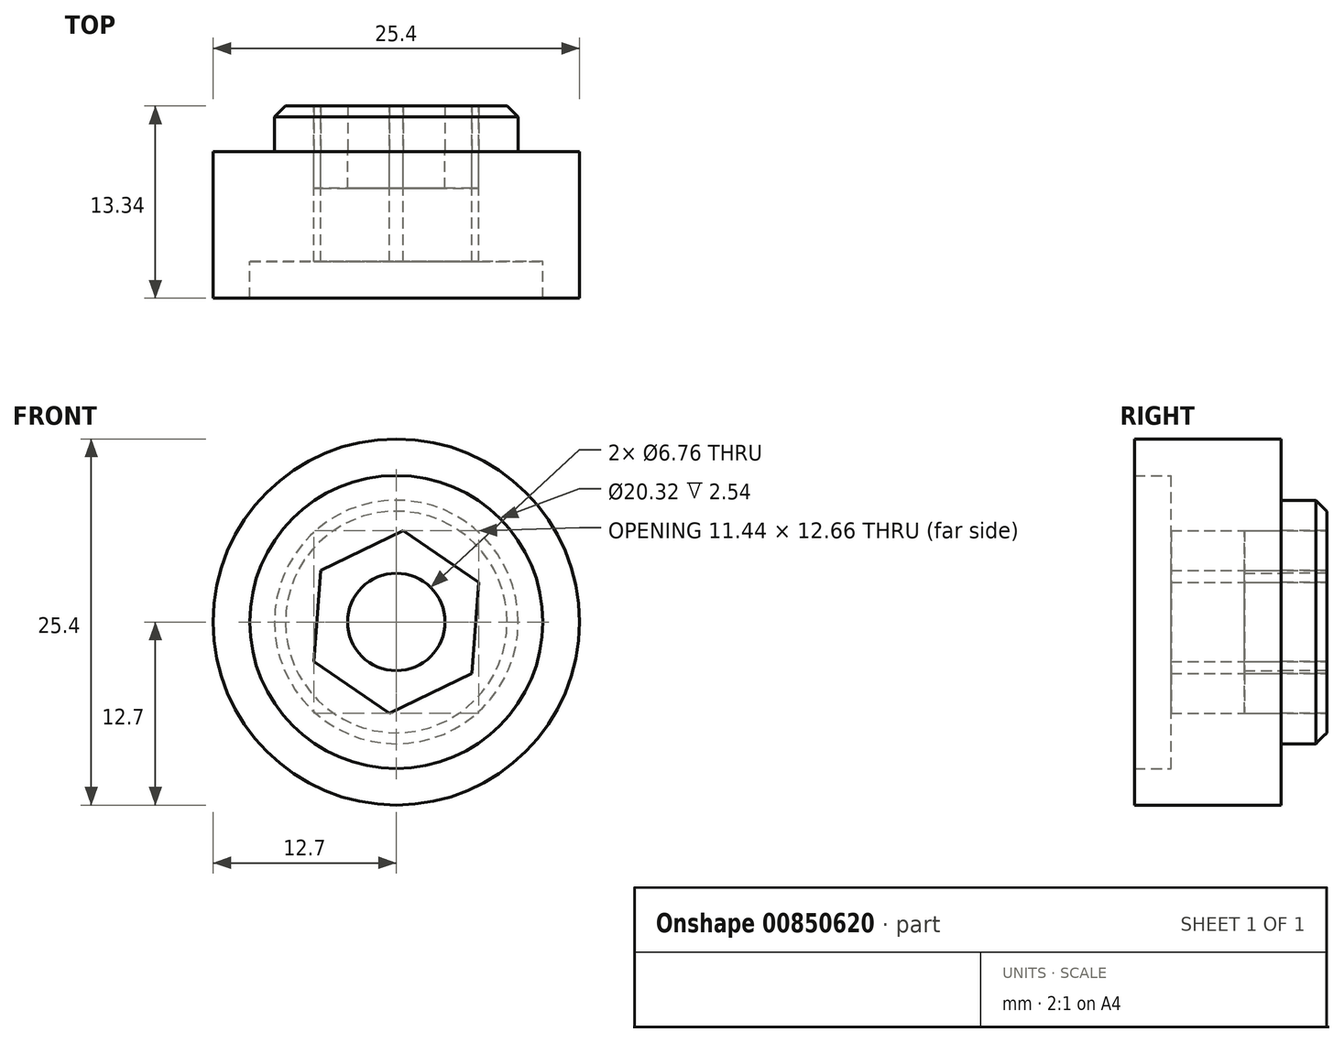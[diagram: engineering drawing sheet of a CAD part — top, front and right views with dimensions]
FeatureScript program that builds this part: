
annotation { "Feature Type Name" : "Feature", "Feature Type Description" : "" }
export const myFeature = defineFeature(function(context is Context, id is Id, definition is map)
    precondition{}
    {
        {
            var Q0;
            Q0=qCreatedBy(makeId("Front.planeOp"),FACE);
            var sketch = newSketch(context, id + "F0", { "sketchPlane" : qUnion([Q0])});
            skCircle(sketch, "E0", {"center": v(0, 0) * mm, "radius": 3.38 * mm});
            skCircle(sketch, "E1.cCircle", {"center": v(0, 0) * mm, "radius": 5.5 * mm, "construction": true});
            skLineSegment(sketch, "E1.0", {"start": v(5.25, -3.58) * mm, "end": v(-0.47, -6.33) * mm});
            skLineSegment(sketch, "E1.1", {"start": v(-0.47, -6.33) * mm, "end": v(-5.72, -2.76) * mm});
            skLineSegment(sketch, "E1.2", {"start": v(-5.72, -2.76) * mm, "end": v(-5.25, 3.58) * mm});
            skLineSegment(sketch, "E1.3", {"start": v(-5.25, 3.58) * mm, "end": v(0.47, 6.33) * mm});
            skLineSegment(sketch, "E1.4", {"start": v(0.47, 6.33) * mm, "end": v(5.72, 2.76) * mm});
            skLineSegment(sketch, "E1.5", {"start": v(5.72, 2.76) * mm, "end": v(5.25, -3.58) * mm});
            skPoint(sketch, "E1.0.midPoint", {"position": v(2.39, -4.95) * mm});
            skCircle(sketch, "E2", {"center": v(0, 0) * mm, "radius": 8.45 * mm});
            skCircle(sketch, "E3", {"center": v(0, 0) * mm, "radius": 10.16 * mm});
            skCircle(sketch, "E4", {"center": v(0, 0) * mm, "radius": 12.7 * mm});
            skSolve(sketch);
        }
        {
            var Q0;
            Q0=makeQuery(id+"F0.imprint","IMPRINT",FACE,{"disambiguationData":[TD([[makeQuery(id+"F0.imprint","IMPRINT",EDGE,{"derivedFrom":sQuery(id+"F0.wireOp",EDGE,"E3")}),-1.0]])]});
            var Q1;
            Q1=sQuery(id+"F0.wireOp",EDGE,"E4");
            extrude(context, id + "F1", {"entities" : qUnion([Q0]), "surfaceEntities" : qUnion([Q1]), "depth" : 10.16 * mm, "offsetDistance" : 25.4 * mm});
        }
        {
            var Q0;
            Q0=makeQuery(id+"F0.imprint","IMPRINT",FACE,{"disambiguationData":[TD([[makeQuery(id+"F0.imprint","IMPRINT",EDGE,{"derivedFrom":sQuery(id+"F0.wireOp",EDGE,"E2")}),-1.0]])]});
            extrude(context, id + "F2", {"entities" : qUnion([Q0]), "operationType" : NewBodyOperationType.ADD, "depth" : 7.62 * mm, "offsetDistance" : 25.4 * mm});
        }
        {
            var Q0;
            Q0=makeQuery(id+"F0.imprint","IMPRINT",FACE,{"disambiguationData":[TD([[makeQuery(id+"F0.imprint","IMPRINT",EDGE,{"derivedFrom":sQuery(id+"F0.wireOp",EDGE,"E1.0")}),1.0]])]});
            var Q1;
            Q1=sQuery(id+"F0.wireOp",EDGE,"E2");
            extrude(context, id + "F3", {"entities" : qUnion([Q0]), "operationType" : NewBodyOperationType.ADD, "surfaceEntities" : qUnion([Q1]), "depth" : 7.62 * mm, "offsetDistance" : 25.4 * mm});
        }
        {
            var Q0;
            Q0=makeQuery(id+"F0.imprint","IMPRINT",FACE,{"disambiguationData":[TD([[makeQuery(id+"F0.imprint","IMPRINT",EDGE,{"derivedFrom":sQuery(id+"F0.wireOp",EDGE,"E1.0")}),1.0]])]});
            var Q1;
            Q1=sQuery(id+"F0.wireOp",EDGE,"E2");
            extrude(context, id + "F4", {"entities" : qUnion([Q0]), "operationType" : NewBodyOperationType.ADD, "surfaceEntities" : qUnion([Q1]), "oppositeDirection" : true, "depth" : 3.17 * mm, "offsetDistance" : 25.4 * mm});
        }
        {
            var Q0;
            Q0=makeQuery(id+"F0.imprint","IMPRINT",FACE,{"disambiguationData":[TD([[makeQuery(id+"F0.imprint","IMPRINT",EDGE,{"derivedFrom":sQuery(id+"F0.wireOp",EDGE,"E0")}),-1.0]])]});
            var Q1;
            Q1=sQuery(id+"F0.wireOp",EDGE,"E0");
            extrude(context, id + "F5", {"entities" : qUnion([Q0]), "surfaceEntities" : qUnion([Q1]), "oppositeDirection" : true, "depth" : 3.17 * mm, "offsetDistance" : 25.4 * mm});
        }
        {
            var Q0;
            Q0=makeQuery(id+"F0.imprint","IMPRINT",FACE,{"disambiguationData":[TD([[makeQuery(id+"F0.imprint","IMPRINT",EDGE,{"derivedFrom":sQuery(id+"F0.wireOp",EDGE,"E0")}),-1.0]])]});
            var Q1;
            Q1=sQuery(id+"F0.wireOp",EDGE,"E0");
            extrude(context, id + "F6", {"entities" : qUnion([Q0]), "surfaceEntities" : qUnion([Q1]), "depth" : 2.54 * mm, "offsetDistance" : 25.4 * mm});
        }
        {
            var Q0;
            Q0=makeQuery(id+"F4.opExtrude","CAP_EDGE",EDGE,{"disambiguationData":[OSD([sQuery(id+"F0.wireOp",EDGE,"E2")])],"isStart":false});
            chamfer(context, id + "F7", {"entities" : qUnion([Q0]), "width" : 0.76 * mm, "tangentPropagation" : true});
        }
    });
